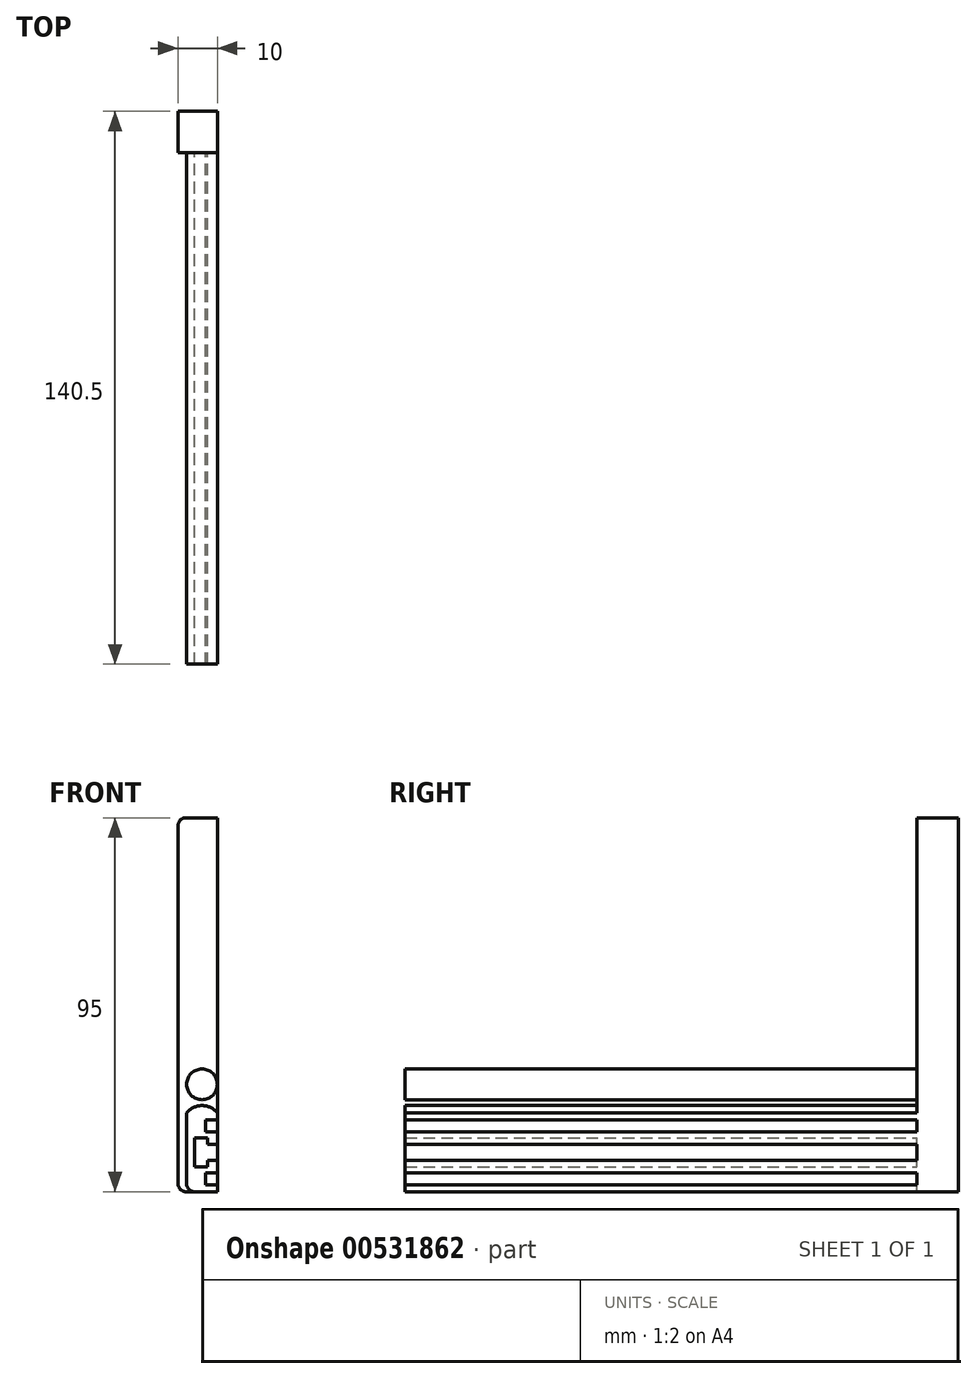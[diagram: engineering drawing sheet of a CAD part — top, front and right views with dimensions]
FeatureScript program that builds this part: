
annotation { "Feature Type Name" : "Feature", "Feature Type Description" : "" }
export const myFeature = defineFeature(function(context is Context, id is Id, definition is map)
    precondition{}
    {
        {
            var Q0;
            Q0=qCreatedBy(makeId("Front.planeOp"),FACE);
            var sketch = newSketch(context, id + "F0", { "sketchPlane" : qUnion([Q0])});
            skLineSegment(sketch, "E0.bottom", {"start": v(0, 0) * mm, "end": v(7.8, 0) * mm});
            skLineSegment(sketch, "E0.top", {"start": v(0, 20) * mm, "end": v(7.8, 20) * mm});
            skLineSegment(sketch, "E0.left", {"start": v(0, 0) * mm, "end": v(0, 20) * mm});
            skLineSegment(sketch, "E0.right", {"start": v(7.8, 0) * mm, "end": v(7.8, 1.75) * mm});
            skLineSegment(sketch, "E1.bottom", {"start": v(7.8, 15.25) * mm, "end": v(4.8, 15.25) * mm});
            skLineSegment(sketch, "E1.top", {"start": v(7.8, 18.25) * mm, "end": v(4.8, 18.25) * mm});
            skLineSegment(sketch, "E1.right", {"start": v(4.8, 15.25) * mm, "end": v(4.8, 18.25) * mm});
            skPoint(sketch, "E1.middle", {"position": v(7.8, 16.75) * mm});
            skLineSegment(sketch, "E2", {"start": v(0, 10) * mm, "end": v(3.65, 10) * mm});
            skPoint(sketch, "E2.endSnap0", {"position": v(0, 10) * mm});
            skLineSegment(sketch, "E3.MirrorCS", {"start": v(7.8, 4.75) * mm, "end": v(4.8, 4.75) * mm});
            skLineSegment(sketch, "E4.MirrorCS", {"start": v(4.8, 4.75) * mm, "end": v(4.8, 1.75) * mm});
            skLineSegment(sketch, "E5.MirrorCS", {"start": v(7.8, 1.75) * mm, "end": v(4.8, 1.75) * mm});
            skLineSegment(sketch, "E6.bottom", {"start": v(5.3, 6.35) * mm, "end": v(2, 6.35) * mm});
            skLineSegment(sketch, "E6.top", {"start": v(5.3, 13.65) * mm, "end": v(2, 13.65) * mm});
            skLineSegment(sketch, "E6.left", {"start": v(5.3, 6.35) * mm, "end": v(5.3, 8) * mm});
            skLineSegment(sketch, "E6.right", {"start": v(2, 6.35) * mm, "end": v(2, 13.65) * mm});
            skPoint(sketch, "E6.middle", {"position": v(3.65, 10) * mm});
            skLineSegment(sketch, "E7.top", {"start": v(5.3, 12) * mm, "end": v(7.8, 12) * mm});
            skLineSegment(sketch, "E8.top", {"start": v(5.3, 8) * mm, "end": v(7.8, 8) * mm});
            skLineSegment(sketch, "E9.trimOffspring", {"start": v(7.8, 12) * mm, "end": v(7.8, 15.25) * mm});
            skLineSegment(sketch, "E10.trimOffspring", {"start": v(7.8, 18.25) * mm, "end": v(7.8, 20) * mm});
            skLineSegment(sketch, "E11.trimOffspring", {"start": v(7.8, 4.75) * mm, "end": v(7.8, 8) * mm});
            skPoint(sketch, "E8.left.start.orphan", {"position": v(5.3, 10) * mm});
            skLineSegment(sketch, "E12.trimOffspring", {"start": v(5.3, 12) * mm, "end": v(5.3, 13.65) * mm});
            skSolve(sketch);
        }
        {
            var Q0;
            Q0=qSketchRegion(id+"F0",true);
            extrude(context, id + "F1", {"entities" : qUnion([Q0]), "depth" : 130 * mm});
        }
        {
            var Q0;
            Q0=makeQuery(id+"F1.opExtrude","CAP_FACE",FACE,{"disambiguationData":[OSD([sQuery(id+"F0.wireOp",EDGE,"E0.bottom"),sQuery(id+"F0.wireOp",EDGE,"E0.top"),sQuery(id+"F0.wireOp",EDGE,"E0.left"),sQuery(id+"F0.wireOp",EDGE,"E0.right"),sQuery(id+"F0.wireOp",EDGE,"E1.bottom"),sQuery(id+"F0.wireOp",EDGE,"E1.top"),sQuery(id+"F0.wireOp",EDGE,"E1.right"),sQuery(id+"F0.wireOp",EDGE,"E3.MirrorCS"),sQuery(id+"F0.wireOp",EDGE,"E4.MirrorCS"),sQuery(id+"F0.wireOp",EDGE,"E5.MirrorCS"),sQuery(id+"F0.wireOp",EDGE,"E6.bottom"),sQuery(id+"F0.wireOp",EDGE,"E6.top"),sQuery(id+"F0.wireOp",EDGE,"E6.left"),sQuery(id+"F0.wireOp",EDGE,"E6.right"),sQuery(id+"F0.wireOp",EDGE,"E7.top"),sQuery(id+"F0.wireOp",EDGE,"E8.top"),sQuery(id+"F0.wireOp",EDGE,"E9.trimOffspring"),sQuery(id+"F0.wireOp",EDGE,"E10.trimOffspring"),sQuery(id+"F0.wireOp",EDGE,"E11.trimOffspring"),sQuery(id+"F0.wireOp",EDGE,"E12.trimOffspring")])],"isStart":true});
            var sketch = newSketch(context, id + "F2", { "sketchPlane" : qUnion([Q0])});
            skLineSegment(sketch, "E13.bottom", {"start": v(-7.8, 20) * mm, "end": v(0, 20) * mm});
            skLineSegment(sketch, "E13.left", {"start": v(-7.8, 20) * mm, "end": v(-7.8, 0) * mm});
            skLineSegment(sketch, "E14.top", {"start": v(-7.8, 95) * mm, "end": v(0, 95) * mm});
            skLineSegment(sketch, "E14.left", {"start": v(-7.8, 20) * mm, "end": v(-7.8, 95) * mm});
            skLineSegment(sketch, "E14.right", {"start": v(0, 20) * mm, "end": v(0, 95) * mm});
            skPoint(sketch, "E13.top.end.orphan", {"position": v(7.2, 0) * mm});
            skLineSegment(sketch, "E15.bottom", {"start": v(0, 20) * mm, "end": v(-7.8, 20) * mm});
            skLineSegment(sketch, "E15.top", {"start": v(0, 0) * mm, "end": v(-7.8, 0) * mm});
            skLineSegment(sketch, "E15.left", {"start": v(0, 20) * mm, "end": v(0, 0) * mm});
            skLineSegment(sketch, "E16.bottom", {"start": v(-7.8, 0) * mm, "end": v(2.2, 0) * mm});
            skLineSegment(sketch, "E16.top", {"start": v(-7.8, 95) * mm, "end": v(2.2, 95) * mm});
            skLineSegment(sketch, "E16.left", {"start": v(-7.8, 0) * mm, "end": v(-7.8, 95) * mm});
            skLineSegment(sketch, "E16.right", {"start": v(2.2, 0) * mm, "end": v(2.2, 95) * mm});
            skSolve(sketch);
        }
        {
            var Q0;
            Q0=qSketchRegion(id+"F2",true);
            extrude(context, id + "F3", {"entities" : qUnion([Q0]), "operationType" : NewBodyOperationType.ADD, "depth" : 10.5 * mm});
        }
        {
            var Q0;
            {var subQ0=sQuery(id+"F2.wireOp",EDGE,"E16.bottom");var subQ1=sQuery(id+"F2.wireOp",EDGE,"E16.left");var subQ2=sQuery(id+"F2.wireOp",EDGE,"E16.top");var subQ3=sQuery(id+"F2.wireOp",EDGE,"E16.right");Q0=makeQuery(id+"F3.boolean.opBoolean","SPLIT",FACE,{"disambiguationData":[TD([makeQuery(id+"F1.opExtrude","SWEPT_FACE",FACE,{"disambiguationData":[OSD([sQuery(id+"F0.wireOp",EDGE,"E0.bottom")])]})])],"derivedFrom":makeQuery(id+"F3.opExtrude","CAP_FACE",FACE,{"disambiguationData":[OSD([subQ0,subQ2,subQ1,subQ3])],"isStart":true})});}
            var sketch = newSketch(context, id + "F4", { "sketchPlane" : qUnion([Q0])});
            skArc(sketch, "E17", {"start": v(7.8, 20) * mm, "mid": v(3.9, 21.87) * mm, "end": v(0, 20) * mm});
            skLineSegment(sketch, "E18", {"start": v(3.9, 20) * mm, "end": v(3.9, 21.87) * mm});
            skLineSegment(sketch, "E19", {"start": v(3.9, 23.37) * mm, "end": v(3.9, 27.27) * mm});
            skCircle(sketch, "E20", {"center": v(3.9, 27.27) * mm, "radius": 3.9 * mm});
            skLineSegment(sketch, "E21", {"start": v(7.8, 20) * mm, "end": v(0, 20) * mm});
            skSolve(sketch);
        }
        {
            var Q0;
            Q0=qSketchRegion(id+"F4",true);
            var Q1;
            Q1=makeQuery(id+"F1.opExtrude","CAP_FACE",FACE,{"disambiguationData":[OSD([sQuery(id+"F0.wireOp",EDGE,"E0.bottom"),sQuery(id+"F0.wireOp",EDGE,"E0.top"),sQuery(id+"F0.wireOp",EDGE,"E0.left"),sQuery(id+"F0.wireOp",EDGE,"E0.right"),sQuery(id+"F0.wireOp",EDGE,"E1.bottom"),sQuery(id+"F0.wireOp",EDGE,"E1.top"),sQuery(id+"F0.wireOp",EDGE,"E1.right"),sQuery(id+"F0.wireOp",EDGE,"E3.MirrorCS"),sQuery(id+"F0.wireOp",EDGE,"E4.MirrorCS"),sQuery(id+"F0.wireOp",EDGE,"E5.MirrorCS"),sQuery(id+"F0.wireOp",EDGE,"E6.bottom"),sQuery(id+"F0.wireOp",EDGE,"E6.top"),sQuery(id+"F0.wireOp",EDGE,"E6.left"),sQuery(id+"F0.wireOp",EDGE,"E6.right"),sQuery(id+"F0.wireOp",EDGE,"E7.top"),sQuery(id+"F0.wireOp",EDGE,"E8.top"),sQuery(id+"F0.wireOp",EDGE,"E9.trimOffspring"),sQuery(id+"F0.wireOp",EDGE,"E10.trimOffspring"),sQuery(id+"F0.wireOp",EDGE,"E11.trimOffspring"),sQuery(id+"F0.wireOp",EDGE,"E12.trimOffspring")])],"isStart":false});
            extrude(context, id + "F5", {"entities" : qUnion([Q0]), "operationType" : NewBodyOperationType.ADD, "endBound" : BoundingType.UP_TO_SURFACE, "endBoundEntityFace" : qUnion([Q1]), "depth" : 25 * mm});
        }
        {
            var Q0;
            Q0=makeQuery(id+"F1.opExtrude","SWEPT_EDGE",EDGE,{"disambiguationData":[OSD([sQuery(id+"F0.wireOp",EDGE,"E0.bottom"),sQuery(id+"F0.wireOp",EDGE,"E0.left")])]});
            var Q1;
            Q1=makeQuery(id+"F3.opExtrude","SWEPT_EDGE",EDGE,{"disambiguationData":[OSD([sQuery(id+"F2.wireOp",EDGE,"E16.top"),sQuery(id+"F2.wireOp",EDGE,"E16.left")])]});
            var Q2;
            Q2=makeQuery(id+"F3.opExtrude","SWEPT_EDGE",EDGE,{"disambiguationData":[OSD([sQuery(id+"F2.wireOp",EDGE,"E16.top"),sQuery(id+"F2.wireOp",EDGE,"E16.right")])]});
            fillet(context, id + "F6", {"entities" : qUnion([Q0, Q1, Q2]), "radius" : 2 * mm, "tangentPropagation" : true, "allowEdgeOverflow" : false});
        }
        {
            var Q0;
            Q0=makeQuery(id+"F3.opExtrude","SWEPT_EDGE",EDGE,{"disambiguationData":[OSD([sQuery(id+"F2.wireOp",EDGE,"E16.bottom"),sQuery(id+"F2.wireOp",EDGE,"E16.right")])]});
            fillet(context, id + "F7", {"entities" : qUnion([Q0]), "radius" : 2 * mm, "tangentPropagation" : true, "allowEdgeOverflow" : false});
        }
    });
